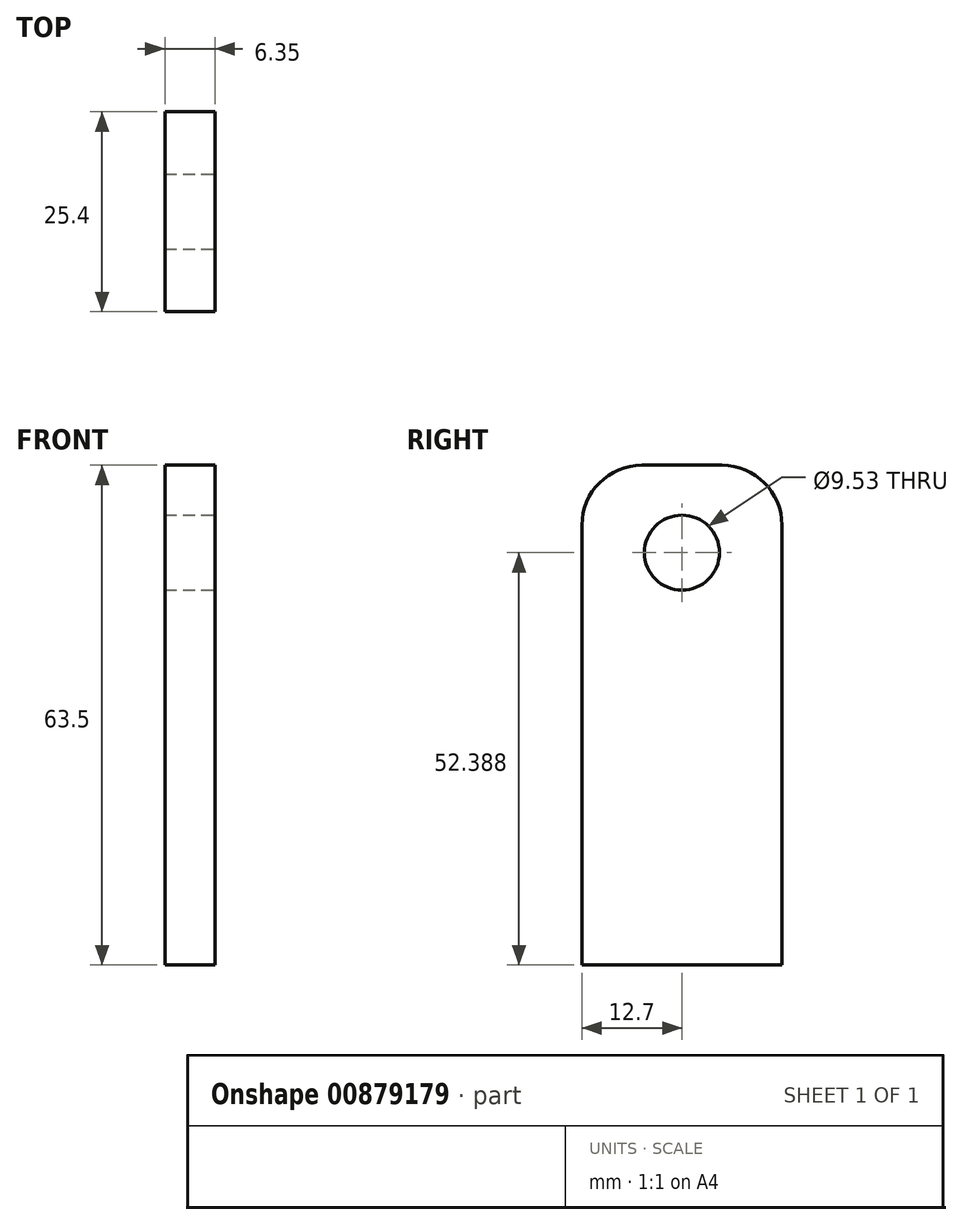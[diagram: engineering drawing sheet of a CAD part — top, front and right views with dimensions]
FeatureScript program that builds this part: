
annotation { "Feature Type Name" : "Feature", "Feature Type Description" : "" }
export const myFeature = defineFeature(function(context is Context, id is Id, definition is map)
    precondition{}
    {
        {
            var Q0;
            Q0=qCreatedBy(makeId("Front.planeOp"),FACE);
            var sketch = newSketch(context, id + "F0", { "sketchPlane" : qUnion([Q0])});
            skLineSegment(sketch, "E0.bottom", {"start": v(0, 0) * mm, "end": v(6.35, 0) * mm});
            skLineSegment(sketch, "E0.top", {"start": v(0, 63.5) * mm, "end": v(6.35, 63.5) * mm});
            skLineSegment(sketch, "E0.left", {"start": v(0, 0) * mm, "end": v(0, 63.5) * mm});
            skLineSegment(sketch, "E0.right", {"start": v(6.35, 0) * mm, "end": v(6.35, 63.5) * mm});
            skSolve(sketch);
        }
        {
            var Q0;
            Q0=qSketchRegion(id+"F0",true);
            extrude(context, id + "F1", {"entities" : qUnion([Q0]), "depth" : 25.4 * mm, "offsetDistance" : 25.4 * mm});
        }
        {
            var Q0;
            Q0=makeQuery(id+"F1.opExtrude","CAP_EDGE",EDGE,{"disambiguationData":[OSD([sQuery(id+"F0.wireOp",EDGE,"E0.top")])],"isStart":false});
            var Q1;
            Q1=makeQuery(id+"F1.opExtrude","CAP_EDGE",EDGE,{"disambiguationData":[OSD([sQuery(id+"F0.wireOp",EDGE,"E0.top")])],"isStart":true});
            fillet(context, id + "F2", {"entities" : qUnion([Q0, Q1]), "radius" : 7.62 * mm, "tangentPropagation" : true, "allowEdgeOverflow" : false});
        }
        {
            var Q0;
            Q0=makeQuery(id+"F1.opExtrude","SWEPT_FACE",FACE,{"disambiguationData":[OSD([sQuery(id+"F0.wireOp",EDGE,"E0.right")])]});
            var sketch = newSketch(context, id + "F3", { "sketchPlane" : qUnion([Q0])});
            skCircle(sketch, "E1", {"center": v(-12.7, 52.39) * mm, "radius": 4.76 * mm});
            skSolve(sketch);
        }
        {
            var Q0;
            Q0=makeQuery(id+"F3.imprint","IMPRINT",FACE,{"disambiguationData":[TD([[makeQuery(id+"F3.imprint","IMPRINT",EDGE,{"derivedFrom":sQuery(id+"F3.wireOp",EDGE,"E1")}),1.0]])]});
            extrude(context, id + "F4", {"entities" : qUnion([Q0]), "operationType" : NewBodyOperationType.REMOVE, "oppositeDirection" : true, "depth" : 25.4 * mm, "offsetDistance" : 25.4 * mm});
        }
    });
